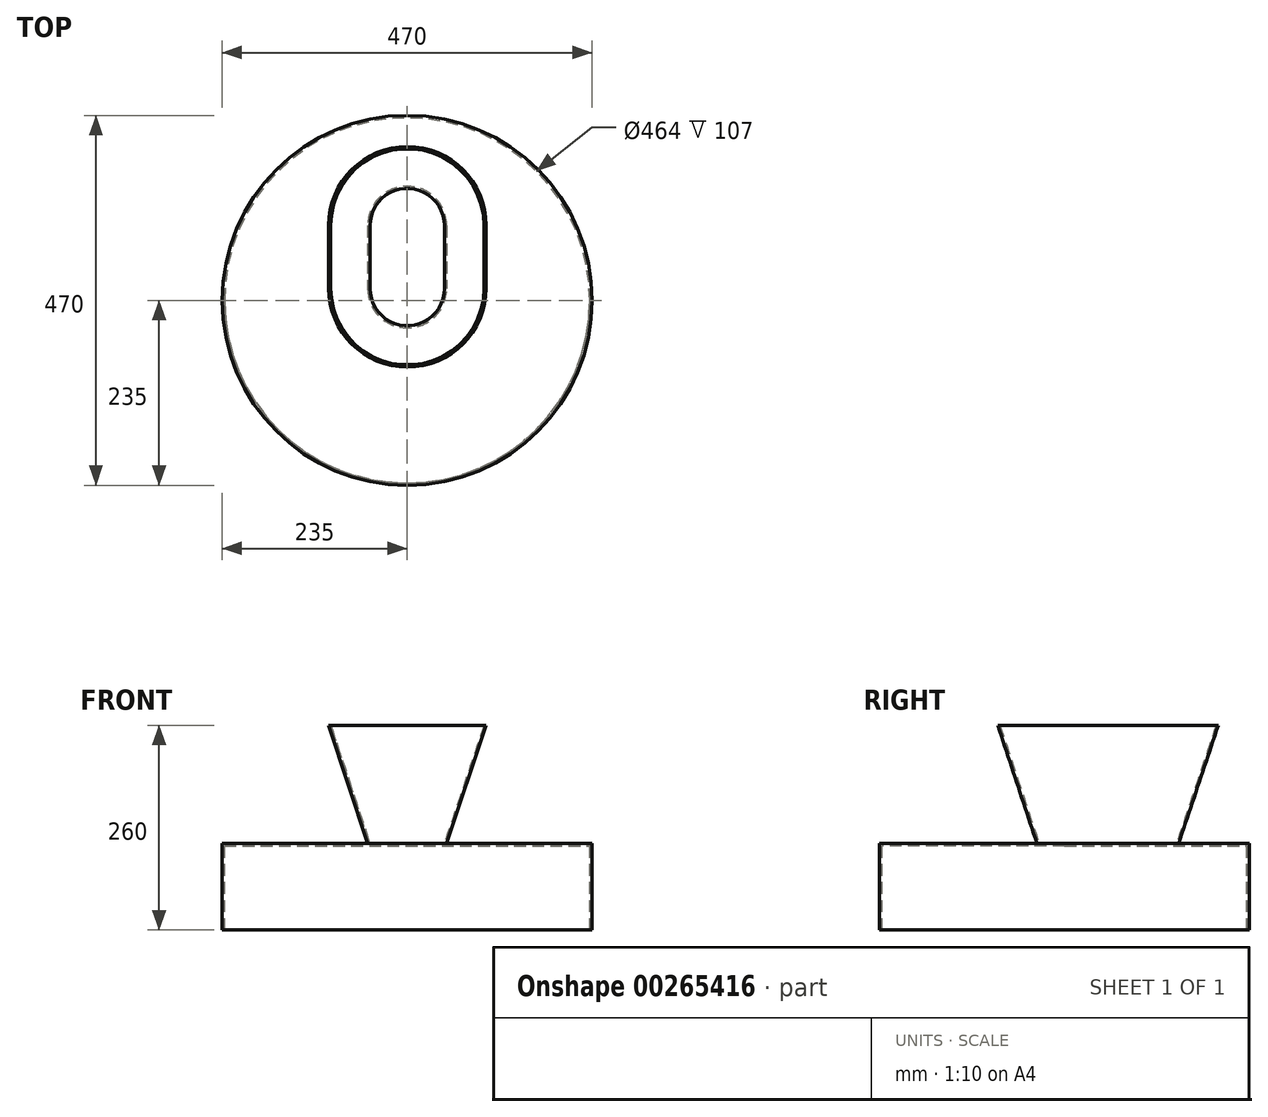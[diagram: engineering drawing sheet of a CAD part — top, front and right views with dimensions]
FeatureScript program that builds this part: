
annotation { "Feature Type Name" : "Feature", "Feature Type Description" : "" }
export const myFeature = defineFeature(function(context is Context, id is Id, definition is map)
    precondition{}
    {
        {
            var Q0;
            Q0=qCreatedBy(makeId("Front.planeOp"),FACE);
            var sketch = newSketch(context, id + "F0", { "sketchPlane" : qUnion([Q0])});
            skLineSegment(sketch, "E0", {"start": v(0, 0) * mm, "end": v(-235, 0) * mm});
            skLineSegment(sketch, "E1", {"start": v(-235, 110) * mm, "end": v(0, 110) * mm});
            skLineSegment(sketch, "E2", {"start": v(-235, 0) * mm, "end": v(-235, 110) * mm});
            skLineSegment(sketch, "E3", {"start": v(0, 110) * mm, "end": v(0, 0) * mm});
            skSolve(sketch);
        }
        {
            var Q0;
            Q0=makeQuery(id+"F0.imprint","IMPRINT",FACE,{"disambiguationData":[TD([[makeQuery(id+"F0.imprint","IMPRINT",EDGE,{"derivedFrom":sQuery(id+"F0.wireOp",EDGE,"E0")}),-1.0]])]});
            var Q1;
            Q1=sQuery(id+"F0.wireOp",EDGE,"E3");
            revolve(context, id + "F1", {"entities" : qUnion([Q0]), "axis" : qUnion([Q1]), "revolveType" : RevolveType.FULL});
        }
        {
            var Q0;
            Q0=makeQuery(id+"F1.opRevolve","SWEPT_FACE",FACE,{"disambiguationData":[OSD([sQuery(id+"F0.wireOp",EDGE,"E0")])]});
            shell(context, id + "F2", {"entities" : qUnion([Q0]), "thickness" : 3 * mm});
        }
        {
            var Q0;
            Q0=makeQuery(id+"F1.opRevolve","SWEPT_FACE",FACE,{"disambiguationData":[OSD([sQuery(id+"F0.wireOp",EDGE,"E1")])]});
            var sketch = newSketch(context, id + "F3", { "sketchPlane" : qUnion([Q0])});
            skCircle(sketch, "E4", {"center": v(0, 0) * mm, "radius": 195 * mm});
            skArc(sketch, "E5", {"start": v(-100, 15) * mm, "mid": v(0, -85) * mm, "end": v(100, 15) * mm});
            skArc(sketch, "E6", {"start": v(100, 95) * mm, "mid": v(0, 195) * mm, "end": v(-100, 95) * mm});
            skLineSegment(sketch, "E7", {"start": v(-100, 95) * mm, "end": v(-100, 15) * mm});
            skLineSegment(sketch, "E8", {"start": v(100, 95) * mm, "end": v(100, 15) * mm});
            skArc(sketch, "E9.0", {"start": v(50, 95) * mm, "mid": v(0, 145) * mm, "end": v(-50, 95) * mm});
            skLineSegment(sketch, "E9.1", {"start": v(50, 95) * mm, "end": v(50, 15) * mm});
            skArc(sketch, "E9.2", {"start": v(-50, 15) * mm, "mid": v(0, -35) * mm, "end": v(50, 15) * mm});
            skLineSegment(sketch, "E9.3", {"start": v(-50, 95) * mm, "end": v(-50, 15) * mm});
            skSolve(sketch);
        }
        {
            var Q0;
            Q0=makeQuery(id+"F3.imprint","IMPRINT",FACE,{"disambiguationData":[TD([[makeQuery(id+"F3.imprint","IMPRINT",EDGE,{"derivedFrom":sQuery(id+"F3.wireOp",EDGE,"E4")}),-1.0]])]});
            cPlane(context, id + "F4", {"entities" : qUnion([Q0]), "cplaneType" : CPlaneType.OFFSET, "offset" : 150 * mm, "width" : 150 * mm, "height" : 150 * mm});
        }
        {
            var Q0;
            Q0=qCreatedBy(id+"F4.planeOp",FACE);
            var sketch = newSketch(context, id + "F5", { "sketchPlane" : qUnion([Q0])});
            skArc(sketch, "E10", {"start": v(-99.68, 15.34) * mm, "mid": v(0.32, -84.66) * mm, "end": v(100.32, 15.34) * mm});
            skArc(sketch, "E11", {"start": v(100.32, 95.34) * mm, "mid": v(0.32, 195.34) * mm, "end": v(-99.68, 95.34) * mm});
            skLineSegment(sketch, "E12", {"start": v(-99.68, 95.34) * mm, "end": v(-99.68, 15.34) * mm});
            skLineSegment(sketch, "E13", {"start": v(100.32, 95.34) * mm, "end": v(100.32, 15.34) * mm});
            skSolve(sketch);
        }
        {
            var Q1;
            Q1=makeQuery(id+"F3.imprint","IMPRINT",FACE,{"disambiguationData":[TD([[makeQuery(id+"F3.imprint","IMPRINT",EDGE,{"derivedFrom":sQuery(id+"F3.wireOp",EDGE,"E9.0")}),1.0]])]});
            var Q2;
            Q2=makeQuery(id+"F5.imprint","IMPRINT",FACE,{"disambiguationData":[TD([[makeQuery(id+"F5.imprint","IMPRINT",EDGE,{"derivedFrom":sQuery(id+"F5.wireOp",EDGE,"E10")}),1.0]])]});
            loft(context, id + "F6", {"operationType" : NewBodyOperationType.ADD, "sheetProfilesArray" : [{ "sheetProfileEntities" : qUnion([Q1]) }, { "sheetProfileEntities" : qUnion([Q2]) }]});
        }
        {
            var Q0;
            Q0=makeQuery(id+"F6.opLoft","CAP_FACE",FACE,{"disambiguationData":[OSD([makeQuery(id+"F5.imprint","IMPRINT",FACE,{"disambiguationData":[TD([[makeQuery(id+"F5.imprint","IMPRINT",EDGE,{"derivedFrom":sQuery(id+"F5.wireOp",EDGE,"E10")}),1.0]])]})])],"isStart":true});
            shell(context, id + "F7", {"entities" : qUnion([Q0]), "thickness" : 2.5 * mm});
        }
    });
